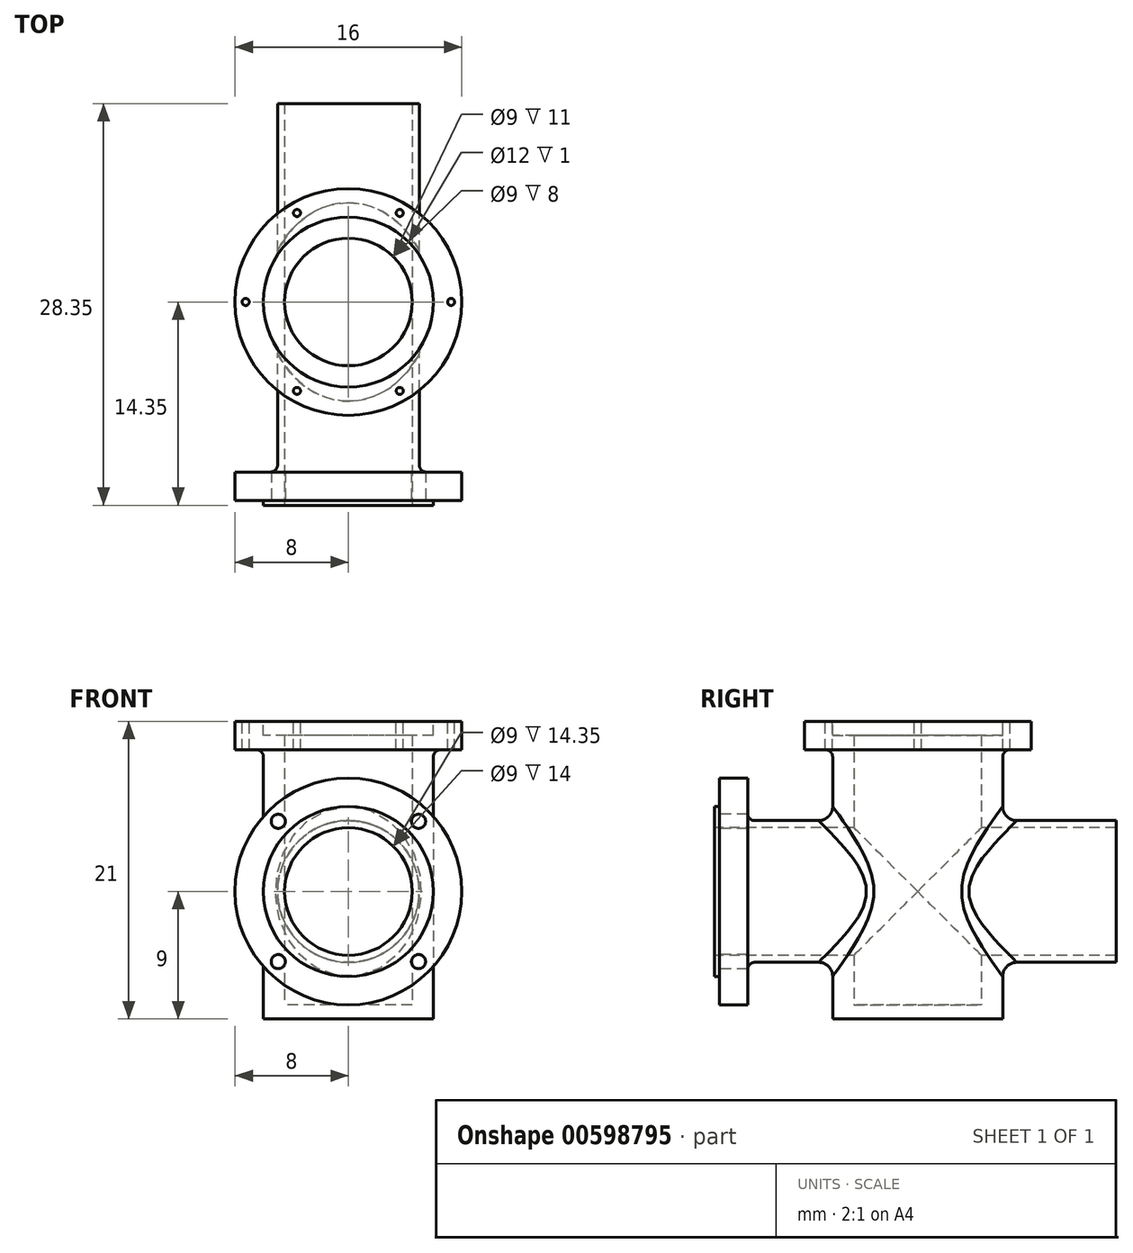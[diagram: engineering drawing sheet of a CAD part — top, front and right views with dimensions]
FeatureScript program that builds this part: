
annotation { "Feature Type Name" : "Feature", "Feature Type Description" : "" }
export const myFeature = defineFeature(function(context is Context, id is Id, definition is map)
    precondition{}
    {
        {
            var Q0;
            Q0=qCreatedBy(makeId("Top.planeOp"),FACE);
            var sketch = newSketch(context, id + "F0", { "sketchPlane" : qUnion([Q0])});
            skCircle(sketch, "E0", {"center": v(0, 0) * mm, "radius": 6 * mm});
            skSolve(sketch);
        }
        {
            var Q0;
            Q0 = qSketchRegion(id + "F0", true);
            extrude(context, id + "F1", {"entities" : qUnion([Q0]), "depth" : 21 * mm, "offsetDistance" : 25 * mm});
        }
        {
            var Q0;
            Q0=qCreatedBy(makeId("Front.planeOp"),FACE);
            var sketch = newSketch(context, id + "F2", { "sketchPlane" : qUnion([Q0])});
            skCircle(sketch, "E1", {"center": v(0, 9) * mm, "radius": 5 * mm});
            skSolve(sketch);
        }
        {
            var Q0;
            Q0 = qSketchRegion(id + "F2", true);
            extrude(context, id + "F3", {"entities" : qUnion([Q0]), "operationType" : NewBodyOperationType.ADD, "depth" : 14 * mm, "offsetDistance" : 25 * mm, "hasSecondDirection" : true, "secondDirectionOppositeDirection" : true, "secondDirectionDepth" : 14 * mm});
        }
        {
            var Q0;
            Q0=makeQuery(id+"F3.opExtrude","CAP_FACE",FACE,{"disambiguationData":[OSD([sQuery(id+"F2.wireOp",EDGE,"E1")])],"isStart":false});
            var sketch = newSketch(context, id + "F4", { "sketchPlane" : qUnion([Q0])});
            skCircle(sketch, "E2", {"center": v(0, 9) * mm, "radius": 8 * mm});
            skSolve(sketch);
        }
        {
            var Q0;
            Q0 = qSketchRegion(id + "F4", true);
            var Q1;
            Q1=sQuery(id+"F4.wireOp",EDGE,"E2");
            extrude(context, id + "F5", {"entities" : qUnion([Q0]), "operationType" : NewBodyOperationType.ADD, "surfaceEntities" : qUnion([Q1]), "oppositeDirection" : true, "depth" : 2 * mm, "offsetDistance" : 25 * mm});
        }
        {
            var Q0;
            Q0=makeQuery(id+"F1.opExtrude","CAP_FACE",FACE,{"disambiguationData":[OSD([sQuery(id+"F0.wireOp",EDGE,"E0")])],"isStart":false});
            var sketch = newSketch(context, id + "F6", { "sketchPlane" : qUnion([Q0])});
            skCircle(sketch, "E3", {"center": v(0, 0) * mm, "radius": 8 * mm});
            skSolve(sketch);
        }
        {
            var Q0;
            Q0 = qSketchRegion(id + "F6", true);
            extrude(context, id + "F7", {"entities" : qUnion([Q0]), "operationType" : NewBodyOperationType.ADD, "oppositeDirection" : true, "depth" : 2 * mm, "offsetDistance" : 25 * mm});
        }
        {
            var Q0;
            Q0=qCreatedBy(makeId("Top.planeOp"),FACE);
            cPlane(context, id + "F8", {"entities" : qUnion([Q0]), "cplaneType" : CPlaneType.OFFSET, "offset" : 1 * mm, "width" : 150 * mm, "height" : 150 * mm});
        }
        {
            var Q0;
            Q0=qCreatedBy(id+"F8.planeOp",FACE);
            var sketch = newSketch(context, id + "F9", { "sketchPlane" : qUnion([Q0])});
            skCircle(sketch, "E4", {"center": v(0, 0) * mm, "radius": 4.5 * mm});
            skSolve(sketch);
        }
        {
            var Q0;
            Q0 = qSketchRegion(id + "F9", true);
            extrude(context, id + "F10", {"entities" : qUnion([Q0]), "operationType" : NewBodyOperationType.REMOVE, "endBound" : BoundingType.THROUGH_ALL, "depth" : 25 * mm, "offsetDistance" : 25 * mm});
        }
        {
            var Q0;
            Q0=makeQuery(id+"F7.boolean.opBoolean","MERGE",FACE,{"derivedFrom":[makeQuery(id+"F1.opExtrude","CAP_FACE",FACE,{"disambiguationData":[OSD([sQuery(id+"F0.wireOp",EDGE,"E0")])],"isStart":false}),makeQuery(id+"F7.opExtrude","CAP_FACE",FACE,{"disambiguationData":[OSD([sQuery(id+"F6.wireOp",EDGE,"E3")])],"isStart":true})]});
            var sketch = newSketch(context, id + "F11", { "sketchPlane" : qUnion([Q0])});
            skCircle(sketch, "E5", {"center": v(0, 0) * mm, "radius": 6 * mm});
            skSolve(sketch);
        }
        {
            var Q0;
            Q0 = qSketchRegion(id + "F11", true);
            extrude(context, id + "F12", {"entities" : qUnion([Q0]), "operationType" : NewBodyOperationType.REMOVE, "oppositeDirection" : true, "depth" : 1 * mm, "offsetDistance" : 25 * mm});
        }
        {
            var Q0;
            Q0=makeQuery(id+"F5.boolean.opBoolean","MERGE",FACE,{"derivedFrom":[makeQuery(id+"F3.opExtrude","CAP_FACE",FACE,{"disambiguationData":[OSD([sQuery(id+"F2.wireOp",EDGE,"E1")])],"isStart":false}),makeQuery(id+"F5.opExtrude","CAP_FACE",FACE,{"disambiguationData":[OSD([sQuery(id+"F4.wireOp",EDGE,"E2")])],"isStart":true})]});
            var sketch = newSketch(context, id + "F13", { "sketchPlane" : qUnion([Q0])});
            skCircle(sketch, "E6", {"center": v(0, 9) * mm, "radius": 6 * mm});
            skSolve(sketch);
        }
        {
            var Q0;
            Q0 = qSketchRegion(id + "F13", true);
            extrude(context, id + "F14", {"entities" : qUnion([Q0]), "operationType" : NewBodyOperationType.ADD, "depth" : .35 * mm, "offsetDistance" : 25 * mm});
        }
        {
            var Q0;
            Q0=qCreatedBy(makeId("Front.planeOp"),FACE);
            var sketch = newSketch(context, id + "F15", { "sketchPlane" : qUnion([Q0])});
            skCircle(sketch, "E7", {"center": v(0, 9) * mm, "radius": 4.5 * mm});
            skSolve(sketch);
        }
        {
            var Q0;
            Q0 = qSketchRegion(id + "F15", true);
            extrude(context, id + "F16", {"entities" : qUnion([Q0]), "operationType" : NewBodyOperationType.REMOVE, "endBound" : BoundingType.THROUGH_ALL, "oppositeDirection" : true, "depth" : 25 * mm, "offsetDistance" : 25 * mm, "hasSecondDirection" : true, "secondDirectionBound" : SecondDirectionBoundingType.THROUGH_ALL, "secondDirectionOppositeDirection" : false, "secondDirectionDepth" : 25 * mm});
        }
        {
            var Q0;
            Q0=makeQuery(id+"F7.boolean.opBoolean","MERGE",FACE,{"derivedFrom":[makeQuery(id+"F1.opExtrude","CAP_FACE",FACE,{"disambiguationData":[OSD([sQuery(id+"F0.wireOp",EDGE,"E0")])],"isStart":false}),makeQuery(id+"F7.opExtrude","CAP_FACE",FACE,{"disambiguationData":[OSD([sQuery(id+"F6.wireOp",EDGE,"E3")])],"isStart":true})]});
            var sketch = newSketch(context, id + "F17", { "sketchPlane" : qUnion([Q0])});
            skCircle(sketch, "E8", {"center": v(0, 0) * mm, "radius": 7.25 * mm, "construction": true});
            skLineSegment(sketch, "E9", {"start": v(0, 0) * mm, "end": v(3.63, 6.28) * mm, "construction": true});
            skCircle(sketch, "E10", {"center": v(3.63, 6.28) * mm, "radius": 0.25 * mm});
            skCircle(sketch, "E11.MirrorC", {"center": v(-3.63, 6.28) * mm, "radius": 0.25 * mm});
            skCircle(sketch, "E12.MirrorC", {"center": v(-3.63, -6.28) * mm, "radius": 0.25 * mm});
            skCircle(sketch, "E13.MirrorC", {"center": v(3.63, -6.28) * mm, "radius": 0.25 * mm});
            skCircle(sketch, "E14", {"center": v(-7.25, 0) * mm, "radius": 0.25 * mm});
            skCircle(sketch, "E15", {"center": v(7.25, 0) * mm, "radius": 0.25 * mm});
            skSolve(sketch);
        }
        {
            var Q0;
            Q0=sQuery(id+"F17.wireOp",VERTEX,"E10.center");
            var Q1;
            Q1=sQuery(id+"F17.wireOp",VERTEX,"E11.MirrorC.center");
            var Q2;
            Q2=sQuery(id+"F17.wireOp",VERTEX,"E14.center");
            var Q3;
            Q3=sQuery(id+"F17.wireOp",VERTEX,"E12.MirrorC.center");
            var Q4;
            Q4=sQuery(id+"F17.wireOp",VERTEX,"E13.MirrorC.center");
            var Q5;
            Q5=sQuery(id+"F17.wireOp",VERTEX,"E15.center");
            var Q6;
            Q6=makeQuery(id+"F1.opExtrude","SWEPT_BODY",BODY,{"disambiguationData":[OSD([sQuery(id+"F0.wireOp",EDGE,"E0")])]});
            hole(context, id + "F18", {"style" : HoleStyle.SIMPLE, "endStyle" : HoleEndStyle.BLIND, "holeDiameter" : .5 * mm, "majorDiameter" : 5 * mm, "holeDepth" : 2 * mm, "isTappedThrough" : true, "tappedDepth" : 12 * mm, "tapClearance" : 3, "startFromSketch" : true, "locations" : qUnion([Q0, Q1, Q2, Q3, Q4, Q5]), "scope" : qUnion([Q6])});
        }
        {
            var Q0;
            Q0=makeQuery(id+"F5.boolean.opBoolean","MERGE",FACE,{"derivedFrom":[makeQuery(id+"F3.opExtrude","CAP_FACE",FACE,{"disambiguationData":[OSD([sQuery(id+"F2.wireOp",EDGE,"E1")])],"isStart":false}),makeQuery(id+"F5.opExtrude","CAP_FACE",FACE,{"disambiguationData":[OSD([sQuery(id+"F4.wireOp",EDGE,"E2")])],"isStart":true})]});
            var sketch = newSketch(context, id + "F19", { "sketchPlane" : qUnion([Q0])});
            skCircle(sketch, "E16", {"center": v(0, 9) * mm, "radius": 7 * mm, "construction": true});
            skLineSegment(sketch, "E17", {"start": v(0, 9) * mm, "end": v(4.95, 13.95) * mm, "construction": true});
            skCircle(sketch, "E18", {"center": v(4.95, 13.95) * mm, "radius": 0.5 * mm});
            skLineSegment(sketch, "E19", {"start": v(0, 9) * mm, "end": v(8, 9) * mm, "construction": true});
            skCircle(sketch, "E20.MirrorC", {"center": v(4.95, 4.05) * mm, "radius": 0.5 * mm});
            skCircle(sketch, "E21.MirrorC", {"center": v(-4.95, 13.95) * mm, "radius": 0.5 * mm});
            skCircle(sketch, "E22.MirrorC", {"center": v(-4.95, 4.05) * mm, "radius": 0.5 * mm});
            skSolve(sketch);
        }
        {
            var Q0;
            Q0=sQuery(id+"F19.wireOp",VERTEX,"E17.end");
            var Q1;
            Q1=sQuery(id+"F19.wireOp",VERTEX,"E20.MirrorC.center");
            var Q2;
            Q2=sQuery(id+"F19.wireOp",VERTEX,"E22.MirrorC.center");
            var Q3;
            Q3=sQuery(id+"F19.wireOp",VERTEX,"E21.MirrorC.center");
            var Q4;
            Q4=makeQuery(id+"F1.opExtrude","SWEPT_BODY",BODY,{"disambiguationData":[OSD([sQuery(id+"F0.wireOp",EDGE,"E0")])]});
            hole(context, id + "F20", {"style" : HoleStyle.SIMPLE, "endStyle" : HoleEndStyle.BLIND, "holeDiameter" : 1 * mm, "majorDiameter" : 5 * mm, "holeDepth" : 2 * mm, "isTappedThrough" : true, "tappedDepth" : 12 * mm, "tapClearance" : 3, "startFromSketch" : true, "locations" : qUnion([Q0, Q1, Q2, Q3]), "scope" : qUnion([Q4])});
        }
        {
            var Q0;
            Q0=makeQuery(id+"F3.boolean.opBoolean","INTERSECT",EDGE,{"disambiguationData":[OD(0.0)],"derivedFrom":[makeQuery(id+"F1.opExtrude","SWEPT_FACE",FACE,{"disambiguationData":[OSD([sQuery(id+"F0.wireOp",EDGE,"E0")])]}),makeQuery(id+"F3.opExtrude","SWEPT_FACE",FACE,{"disambiguationData":[OSD([sQuery(id+"F2.wireOp",EDGE,"E1")])]})]});
            var Q1;
            Q1=makeQuery(id+"F3.boolean.opBoolean","INTERSECT",EDGE,{"disambiguationData":[OD(1.0)],"derivedFrom":[makeQuery(id+"F1.opExtrude","SWEPT_FACE",FACE,{"disambiguationData":[OSD([sQuery(id+"F0.wireOp",EDGE,"E0")])]}),makeQuery(id+"F3.opExtrude","SWEPT_FACE",FACE,{"disambiguationData":[OSD([sQuery(id+"F2.wireOp",EDGE,"E1")])]})]});
            fillet(context, id + "F21", {"entities" : qUnion([Q0, Q1]), "radius" : 1 * mm, "tangentPropagation" : true, "allowEdgeOverflow" : false});
        }
        {
            var Q0;
            {var subQ0=sQuery(id+"F2.wireOp",EDGE,"E1");Q0=makeQuery(id+"F4wcatQ1u9RNav0_1.1.F5.boolean.opBoolean","INTERSECT",EDGE,{"derivedFrom":[makeQuery(id+"F3.boolean.opBoolean","SPLIT",FACE,{"disambiguationData":[TD([makeQuery(id+"F3.opExtrude","CAP_FACE",FACE,{"disambiguationData":[OSD([subQ0])],"isStart":true})])],"derivedFrom":makeQuery(id+"F3.opExtrude","SWEPT_FACE",FACE,{"disambiguationData":[OSD([subQ0])]})}),makeQuery(id+"F4wcatQ1u9RNav0_1.1.F5.opExtrude","CAP_FACE",FACE,{"disambiguationData":[OSD([sQuery(id+"F4.wireOp",EDGE,"E2")])],"isStart":false})]});}
            var Q1;
            Q1=makeQuery(id+"F7.boolean.opBoolean","INTERSECT",EDGE,{"derivedFrom":[makeQuery(id+"F1.opExtrude","SWEPT_FACE",FACE,{"disambiguationData":[OSD([sQuery(id+"F0.wireOp",EDGE,"E0")])]}),makeQuery(id+"F7.opExtrude","CAP_FACE",FACE,{"disambiguationData":[OSD([sQuery(id+"F6.wireOp",EDGE,"E3")])],"isStart":false})]});
            var Q2;
            {var subQ0=sQuery(id+"F2.wireOp",EDGE,"E1");Q2=makeQuery(id+"F5.boolean.opBoolean","INTERSECT",EDGE,{"derivedFrom":[makeQuery(id+"F3.boolean.opBoolean","SPLIT",FACE,{"disambiguationData":[TD([makeQuery(id+"F3.opExtrude","CAP_FACE",FACE,{"disambiguationData":[OSD([subQ0])],"isStart":false})])],"derivedFrom":makeQuery(id+"F3.opExtrude","SWEPT_FACE",FACE,{"disambiguationData":[OSD([subQ0])]})}),makeQuery(id+"F5.opExtrude","CAP_FACE",FACE,{"disambiguationData":[OSD([sQuery(id+"F4.wireOp",EDGE,"E2")])],"isStart":false})]});}
            fillet(context, id + "F22", {"entities" : qUnion([Q0, Q1, Q2]), "radius" : .5 * mm, "tangentPropagation" : true, "allowEdgeOverflow" : false});
        }
    });
